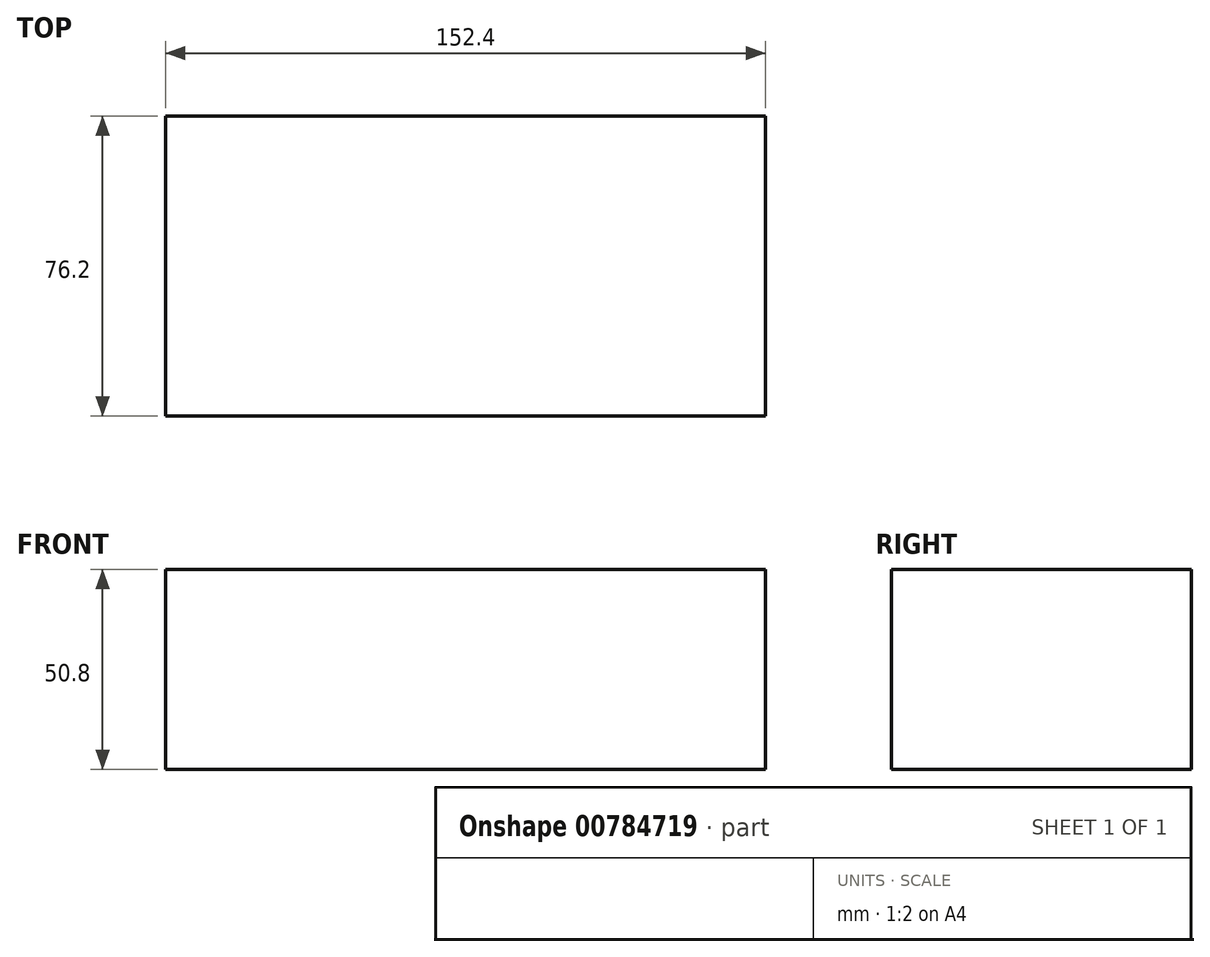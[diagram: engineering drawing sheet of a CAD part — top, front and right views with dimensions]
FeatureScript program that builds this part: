
annotation { "Feature Type Name" : "Feature", "Feature Type Description" : "" }
export const myFeature = defineFeature(function(context is Context, id is Id, definition is map)
    precondition{}
    {
        {
            var Q0;
            Q0=qCreatedBy(makeId("Front.planeOp"),FACE);
            var sketch = newSketch(context, id + "F0", { "sketchPlane" : qUnion([Q0])});
            skLineSegment(sketch, "E0.bottom", {"start": v(76.2, 25.4) * mm, "end": v(-76.2, 25.4) * mm});
            skLineSegment(sketch, "E0.top", {"start": v(76.2, -25.4) * mm, "end": v(-76.2, -25.4) * mm});
            skLineSegment(sketch, "E0.left", {"start": v(76.2, 25.4) * mm, "end": v(76.2, -25.4) * mm});
            skLineSegment(sketch, "E0.right", {"start": v(-76.2, 25.4) * mm, "end": v(-76.2, -25.4) * mm});
            skPoint(sketch, "E0.middle", {"position": v(0, 0) * mm});
            skSolve(sketch);
        }
        {
            var Q0;
            Q0 = qSketchRegion(id + "F0", true);
            extrude(context, id + "F1", {"entities" : qUnion([Q0]), "depth" : 76.2 * mm, "offsetDistance" : 25.4 * mm});
        }
    });
